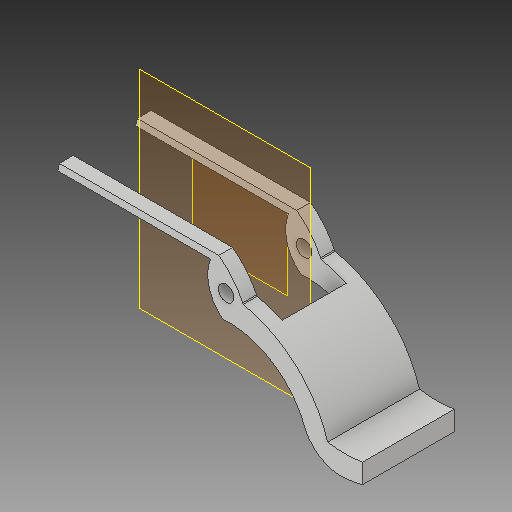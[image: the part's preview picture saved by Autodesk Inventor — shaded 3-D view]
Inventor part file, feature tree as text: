
AUTODESK INVENTOR PART (.ipt)
format: ipt  version: 2017 (Build 210142000, 142)  size: 161,280 bytes
history: native  units: mm
features: other x6, extrude x2, sketch x2, mirror x1
ambient origin geometry x8: Origin, YZ Plane, XZ Plane, XY Plane, X Axis, Y Axis, Z Axis, Center Point
bodies: Solide1 (feature_tree)
feature tree (11):
  other  "Plan de construction1"
  extrude  "Extrusion1"  Depth=4.0mm TaperAngle=0.0deg
  other  "Plan de construction2"
  mirror  "Symétrie1"
  extrude  "Extrusion5"  Depth=9.25mm
  sketch  "Esquisse1"
  other  "Référence1"
  sketch  "Esquisse4"
  other  "<userpath>\Documents\Modele 3D\Lanceur boule\Ensemble_Lanceur.iam"
  other  "Ensemble_Lanceur.iam"
  other  "enclenchement:1"
